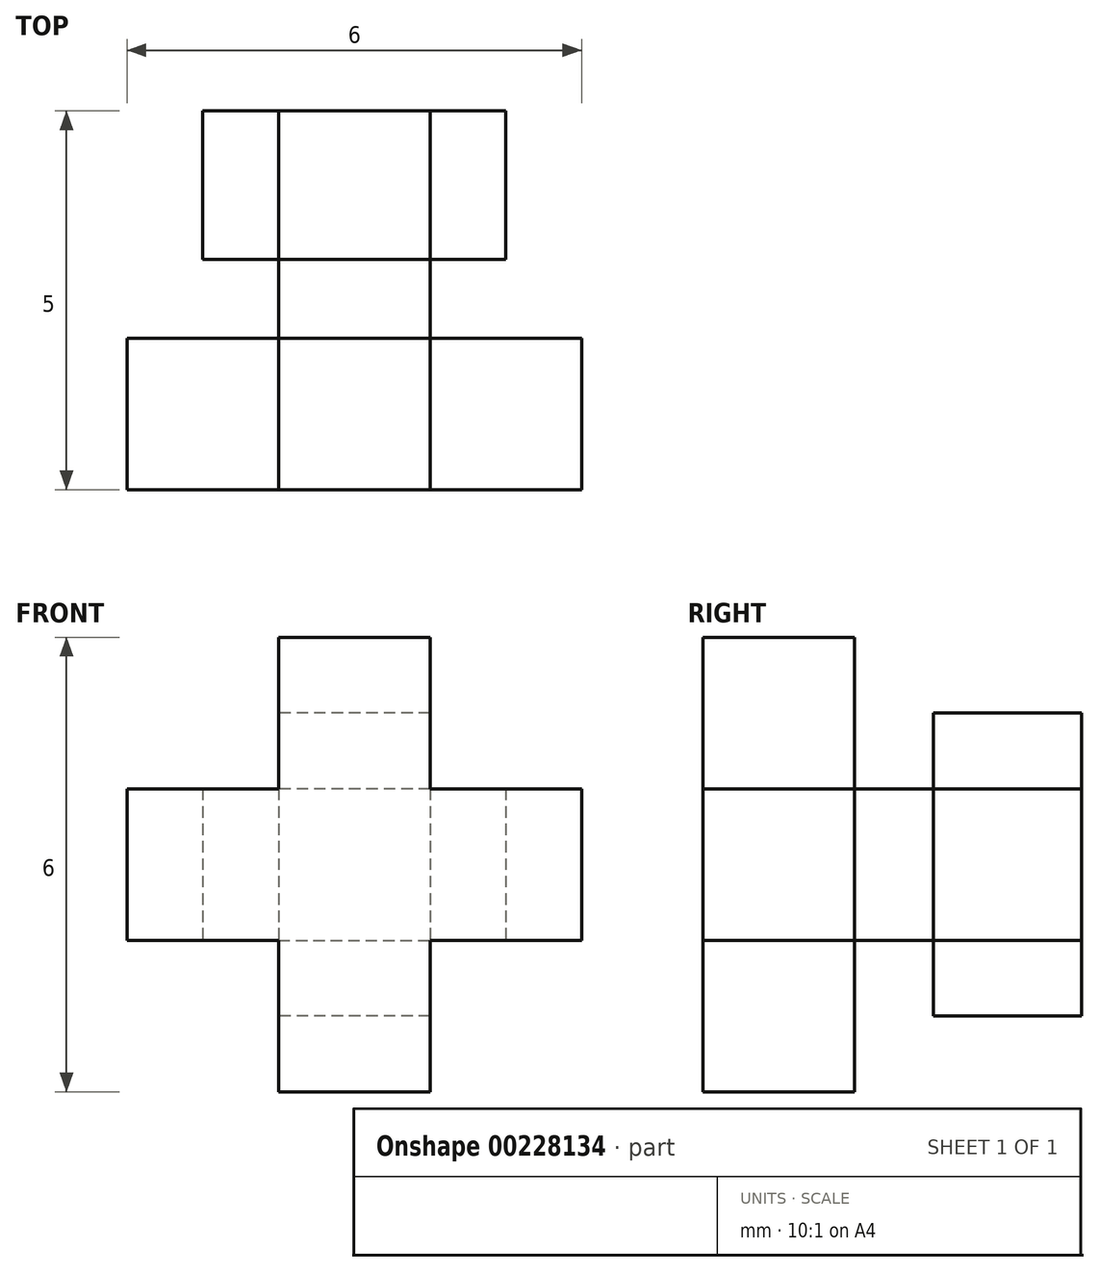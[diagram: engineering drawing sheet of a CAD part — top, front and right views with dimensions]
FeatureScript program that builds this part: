
annotation { "Feature Type Name" : "Feature", "Feature Type Description" : "" }
export const myFeature = defineFeature(function(context is Context, id is Id, definition is map)
    precondition{}
    {
        {
            var Q0;
            Q0=qCreatedBy(makeId("Front.planeOp"),FACE);
            var sketch = newSketch(context, id + "F0", { "sketchPlane" : qUnion([Q0])});
            skLineSegment(sketch, "E0.bottom", {"start": v(1, 1) * mm, "end": v(-1, 1) * mm});
            skLineSegment(sketch, "E0.top", {"start": v(1, -1) * mm, "end": v(-1, -1) * mm});
            skLineSegment(sketch, "E0.left", {"start": v(1, 1) * mm, "end": v(1, -1) * mm});
            skLineSegment(sketch, "E0.right", {"start": v(-1, 1) * mm, "end": v(-1, -1) * mm});
            skPoint(sketch, "E0.middle", {"position": v(0, 0) * mm});
            skSolve(sketch);
        }
        {
            var Q0;
            Q0 = qSketchRegion(id + "F0", true);
            extrude(context, id + "F1", {"entities" : qUnion([Q0]), "depth" : 5 * mm});
        }
        {
            var Q0;
            Q0=makeQuery(id+"F1.opExtrude","SWEPT_FACE",FACE,{"disambiguationData":[OSD([sQuery(id+"F0.wireOp",EDGE,"E0.top")])]});
            var sketch = newSketch(context, id + "F2", { "sketchPlane" : qUnion([Q0])});
            skLineSegment(sketch, "E1.bottom", {"start": v(-1, 5) * mm, "end": v(1, 5) * mm});
            skLineSegment(sketch, "E1.top", {"start": v(-1, 3) * mm, "end": v(1, 3) * mm});
            skLineSegment(sketch, "E1.left", {"start": v(-1, 5) * mm, "end": v(-1, 3) * mm});
            skLineSegment(sketch, "E1.right", {"start": v(1, 5) * mm, "end": v(1, 3) * mm});
            skSolve(sketch);
        }
        {
            var Q0;
            Q0 = qSketchRegion(id + "F2", true);
            extrude(context, id + "F3", {"entities" : qUnion([Q0]), "operationType" : NewBodyOperationType.ADD, "depth" : 2 * mm});
        }
        {
            var Q0;
            Q0=makeQuery(id+"F1.opExtrude","SWEPT_FACE",FACE,{"disambiguationData":[OSD([sQuery(id+"F0.wireOp",EDGE,"E0.top")])]});
            var sketch = newSketch(context, id + "F4", { "sketchPlane" : qUnion([Q0])});
            skLineSegment(sketch, "E2.bottom", {"start": v(-1, 0) * mm, "end": v(1, 0) * mm});
            skLineSegment(sketch, "E2.top", {"start": v(-1, 1.96) * mm, "end": v(1, 1.96) * mm});
            skLineSegment(sketch, "E2.left", {"start": v(-1, 0) * mm, "end": v(-1, 1.96) * mm});
            skLineSegment(sketch, "E2.right", {"start": v(1, 0) * mm, "end": v(1, 1.96) * mm});
            skSolve(sketch);
        }
        {
            var Q0;
            Q0 = qSketchRegion(id + "F4", true);
            extrude(context, id + "F5", {"entities" : qUnion([Q0]), "operationType" : NewBodyOperationType.ADD, "depth" : 1 * mm});
        }
        {
            var Q0;
            Q0=makeQuery(id+"F5.boolean.opBoolean","MERGE",FACE,{"derivedFrom":[makeQuery(id+"F3.boolean.opBoolean","MERGE",FACE,{"derivedFrom":[makeQuery(id+"F1.opExtrude","SWEPT_FACE",FACE,{"disambiguationData":[OSD([sQuery(id+"F0.wireOp",EDGE,"E0.right")])]}),makeQuery(id+"F3.opExtrude","SWEPT_FACE",FACE,{"disambiguationData":[OSD([sQuery(id+"F2.wireOp",EDGE,"E1.left")])]})]}),makeQuery(id+"F5.opExtrude","SWEPT_FACE",FACE,{"disambiguationData":[OSD([sQuery(id+"F4.wireOp",EDGE,"E2.left")])]})]});
            var sketch = newSketch(context, id + "F6", { "sketchPlane" : qUnion([Q0])});
            skLineSegment(sketch, "E3.bottom", {"start": v(0, 1) * mm, "end": v(1.96, 1) * mm});
            skLineSegment(sketch, "E3.top", {"start": v(0, -1) * mm, "end": v(1.96, -1) * mm});
            skLineSegment(sketch, "E3.left", {"start": v(0, 1) * mm, "end": v(0, -1) * mm});
            skLineSegment(sketch, "E3.right", {"start": v(1.96, 1) * mm, "end": v(1.96, -1) * mm});
            skSolve(sketch);
        }
        {
            var Q0;
            Q0 = qSketchRegion(id + "F6", true);
            extrude(context, id + "F7", {"entities" : qUnion([Q0]), "operationType" : NewBodyOperationType.ADD, "depth" : 1 * mm});
        }
        {
            var Q0;
            {var subQ0=sQuery(id+"F2.wireOp",EDGE,"E1.left");var subQ1=makeQuery(id+"F3.opExtrude","SWEPT_FACE",FACE,{"disambiguationData":[OSD([subQ0])]});var subQ4=sQuery(id+"F0.wireOp",EDGE,"E0.bottom");var subQ5=sQuery(id+"F0.wireOp",EDGE,"E0.right");var subQ7=makeQuery(id+"F5.opExtrude","SWEPT_FACE",FACE,{"disambiguationData":[OSD([sQuery(id+"F4.wireOp",EDGE,"E2.left")])]});var subQ8=makeQuery(id+"F1.opExtrude","SWEPT_FACE",FACE,{"disambiguationData":[OSD([subQ5])]});Q0=makeQuery(id+"F7.boolean.opBoolean","SPLIT",FACE,{"disambiguationData":[TD([makeQuery(id+"F1.opExtrude","SWEPT_FACE",FACE,{"disambiguationData":[OSD([subQ4])]})])],"derivedFrom":makeQuery(id+"F5.boolean.opBoolean","MERGE",FACE,{"derivedFrom":[makeQuery(id+"F3.boolean.opBoolean","MERGE",FACE,{"derivedFrom":[subQ8,subQ1]}),subQ7]})});}
            var sketch = newSketch(context, id + "F8", { "sketchPlane" : qUnion([Q0])});
            skLineSegment(sketch, "E4.bottom", {"start": v(5, 1) * mm, "end": v(3, 1) * mm});
            skLineSegment(sketch, "E4.top", {"start": v(5, -1) * mm, "end": v(3, -1) * mm});
            skLineSegment(sketch, "E4.left", {"start": v(5, 1) * mm, "end": v(5, -1) * mm});
            skLineSegment(sketch, "E4.right", {"start": v(3, 1) * mm, "end": v(3, -1) * mm});
            skSolve(sketch);
        }
        {
            var Q0;
            Q0 = qSketchRegion(id + "F8", true);
            extrude(context, id + "F9", {"entities" : qUnion([Q0]), "operationType" : NewBodyOperationType.ADD, "depth" : 2 * mm});
        }
        {
            var Q0;
            Q0=makeQuery(id+"F9.boolean.opBoolean","MERGE",FACE,{"derivedFrom":[makeQuery(id+"F7.boolean.opBoolean","MERGE",FACE,{"derivedFrom":[makeQuery(id+"F1.opExtrude","SWEPT_FACE",FACE,{"disambiguationData":[OSD([sQuery(id+"F0.wireOp",EDGE,"E0.bottom")])]}),makeQuery(id+"F7.opExtrude","SWEPT_FACE",FACE,{"disambiguationData":[OSD([sQuery(id+"F6.wireOp",EDGE,"E3.bottom")])]})]}),makeQuery(id+"F9.opExtrude","SWEPT_FACE",FACE,{"disambiguationData":[OSD([sQuery(id+"F8.wireOp",EDGE,"E4.bottom")])]})]});
            var sketch = newSketch(context, id + "F10", { "sketchPlane" : qUnion([Q0])});
            skLineSegment(sketch, "E5.bottom", {"start": v(1, -5) * mm, "end": v(-1, -5) * mm});
            skLineSegment(sketch, "E5.top", {"start": v(1, -3) * mm, "end": v(-1, -3) * mm});
            skLineSegment(sketch, "E5.left", {"start": v(1, -5) * mm, "end": v(1, -3) * mm});
            skLineSegment(sketch, "E5.right", {"start": v(-1, -5) * mm, "end": v(-1, -3) * mm});
            skSolve(sketch);
        }
        {
            var Q0;
            Q0 = qSketchRegion(id + "F10", true);
            extrude(context, id + "F11", {"entities" : qUnion([Q0]), "operationType" : NewBodyOperationType.ADD, "depth" : 2 * mm});
        }
        {
            var Q0;
            {var subQ0=sQuery(id+"F6.wireOp",EDGE,"E3.bottom");var subQ1=makeQuery(id+"F7.opExtrude","SWEPT_FACE",FACE,{"disambiguationData":[OSD([subQ0])]});var subQ2=sQuery(id+"F0.wireOp",EDGE,"E0.left");var subQ3=sQuery(id+"F0.wireOp",EDGE,"E0.bottom");var subQ4=makeQuery(id+"F1.opExtrude","SWEPT_FACE",FACE,{"disambiguationData":[OSD([subQ3])]});var subQ8=makeQuery(id+"F9.opExtrude","SWEPT_FACE",FACE,{"disambiguationData":[OSD([sQuery(id+"F8.wireOp",EDGE,"E4.bottom")])]});Q0=makeQuery(id+"F11.boolean.opBoolean","SPLIT",FACE,{"disambiguationData":[TD([makeQuery(id+"F1.opExtrude","SWEPT_FACE",FACE,{"disambiguationData":[OSD([subQ2])]})])],"derivedFrom":makeQuery(id+"F9.boolean.opBoolean","MERGE",FACE,{"derivedFrom":[makeQuery(id+"F7.boolean.opBoolean","MERGE",FACE,{"derivedFrom":[subQ4,subQ1]}),subQ8]})});}
            var sketch = newSketch(context, id + "F12", { "sketchPlane" : qUnion([Q0])});
            skLineSegment(sketch, "E6.bottom", {"start": v(1, 0) * mm, "end": v(-1, 0) * mm});
            skLineSegment(sketch, "E6.top", {"start": v(1, -1.96) * mm, "end": v(-1, -1.96) * mm});
            skLineSegment(sketch, "E6.left", {"start": v(1, 0) * mm, "end": v(1, -1.96) * mm});
            skLineSegment(sketch, "E6.right", {"start": v(-1, 0) * mm, "end": v(-1, -1.96) * mm});
            skSolve(sketch);
        }
        {
            var Q0;
            Q0 = qSketchRegion(id + "F12", true);
            extrude(context, id + "F13", {"entities" : qUnion([Q0]), "operationType" : NewBodyOperationType.ADD, "depth" : 1 * mm});
        }
        {
            var Q0;
            Q0=makeQuery(id+"F13.boolean.opBoolean","MERGE",FACE,{"derivedFrom":[makeQuery(id+"F11.boolean.opBoolean","MERGE",FACE,{"derivedFrom":[makeQuery(id+"F5.boolean.opBoolean","MERGE",FACE,{"derivedFrom":[makeQuery(id+"F3.boolean.opBoolean","MERGE",FACE,{"derivedFrom":[makeQuery(id+"F1.opExtrude","SWEPT_FACE",FACE,{"disambiguationData":[OSD([sQuery(id+"F0.wireOp",EDGE,"E0.left")])]}),makeQuery(id+"F3.opExtrude","SWEPT_FACE",FACE,{"disambiguationData":[OSD([sQuery(id+"F2.wireOp",EDGE,"E1.right")])]})]}),makeQuery(id+"F5.opExtrude","SWEPT_FACE",FACE,{"disambiguationData":[OSD([sQuery(id+"F4.wireOp",EDGE,"E2.right")])]})]}),makeQuery(id+"F11.opExtrude","SWEPT_FACE",FACE,{"disambiguationData":[OSD([sQuery(id+"F10.wireOp",EDGE,"E5.left")])]})]}),makeQuery(id+"F13.opExtrude","SWEPT_FACE",FACE,{"disambiguationData":[OSD([sQuery(id+"F12.wireOp",EDGE,"E6.left")])]})]});
            var sketch = newSketch(context, id + "F14", { "sketchPlane" : qUnion([Q0])});
            skLineSegment(sketch, "E7.bottom", {"start": v(-3, -1) * mm, "end": v(-5, -1) * mm});
            skLineSegment(sketch, "E7.top", {"start": v(-3, 1) * mm, "end": v(-5, 1) * mm});
            skLineSegment(sketch, "E7.left", {"start": v(-3, -1) * mm, "end": v(-3, 1) * mm});
            skLineSegment(sketch, "E7.right", {"start": v(-5, -1) * mm, "end": v(-5, 1) * mm});
            skSolve(sketch);
        }
        {
            var Q0;
            Q0 = qSketchRegion(id + "F14", true);
            extrude(context, id + "F15", {"entities" : qUnion([Q0]), "operationType" : NewBodyOperationType.ADD, "depth" : 2 * mm});
        }
        {
            var Q0;
            {var subQ1=sQuery(id+"F4.wireOp",EDGE,"E2.bottom");var subQ2=sQuery(id+"F4.wireOp",EDGE,"E2.right");var subQ5=makeQuery(id+"F3.opExtrude","SWEPT_FACE",FACE,{"disambiguationData":[OSD([sQuery(id+"F2.wireOp",EDGE,"E1.right")])]});var subQ6=sQuery(id+"F12.wireOp",EDGE,"E6.left");var subQ8=sQuery(id+"F0.wireOp",EDGE,"E0.left");var subQ10=makeQuery(id+"F11.opExtrude","SWEPT_FACE",FACE,{"disambiguationData":[OSD([sQuery(id+"F10.wireOp",EDGE,"E5.left")])]});var subQ11=makeQuery(id+"F5.opExtrude","SWEPT_FACE",FACE,{"disambiguationData":[OSD([subQ2])]});var subQ12=makeQuery(id+"F1.opExtrude","SWEPT_FACE",FACE,{"disambiguationData":[OSD([subQ8])]});var subQ13=makeQuery(id+"F13.opExtrude","SWEPT_FACE",FACE,{"disambiguationData":[OSD([subQ6])]});Q0=makeQuery(id+"F15.boolean.opBoolean","SPLIT",FACE,{"disambiguationData":[TD([makeQuery(id+"F5.opExtrude","SWEPT_FACE",FACE,{"disambiguationData":[OSD([subQ1])]})])],"derivedFrom":makeQuery(id+"F13.boolean.opBoolean","MERGE",FACE,{"derivedFrom":[makeQuery(id+"F11.boolean.opBoolean","MERGE",FACE,{"derivedFrom":[makeQuery(id+"F5.boolean.opBoolean","MERGE",FACE,{"derivedFrom":[makeQuery(id+"F3.boolean.opBoolean","MERGE",FACE,{"derivedFrom":[subQ12,subQ5]}),subQ11]}),subQ10]}),subQ13]})});}
            var sketch = newSketch(context, id + "F16", { "sketchPlane" : qUnion([Q0])});
            skLineSegment(sketch, "E8.bottom", {"start": v(-1.96, 1) * mm, "end": v(0, 1) * mm});
            skLineSegment(sketch, "E8.top", {"start": v(-1.96, -1) * mm, "end": v(0, -1) * mm});
            skLineSegment(sketch, "E8.left", {"start": v(-1.96, 1) * mm, "end": v(-1.96, -1) * mm});
            skLineSegment(sketch, "E8.right", {"start": v(0, 1) * mm, "end": v(0, -1) * mm});
            skSolve(sketch);
        }
        {
            var Q0;
            Q0 = qSketchRegion(id + "F16", true);
            extrude(context, id + "F17", {"entities" : qUnion([Q0]), "operationType" : NewBodyOperationType.ADD, "depth" : 1 * mm});
        }
    });
